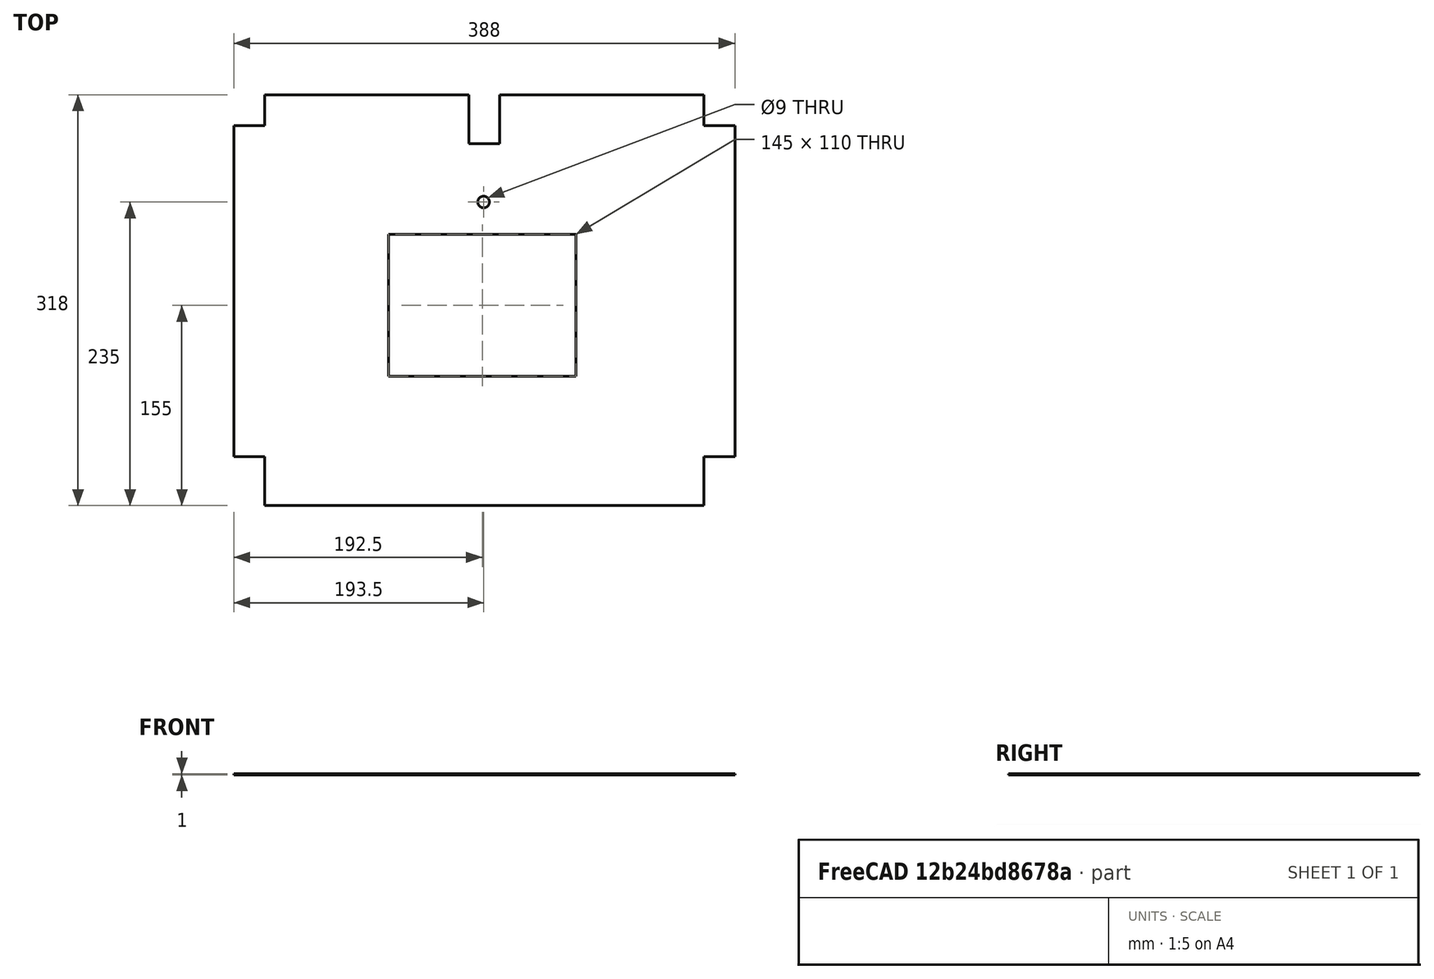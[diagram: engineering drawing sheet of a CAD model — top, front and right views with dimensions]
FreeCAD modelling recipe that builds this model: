
FCSTD DOCUMENT  (FreeCAD 0.15R4671 (Git))
Label: Plataforma
License: All rights reserved
LicenseURL: http://es.wikipedia.org/wiki/Todos_los_derechos_reservados
objects: Part::Box×7, Part::MultiFuse×2, Part::Cylinder×1, Part::Cut×1
note: 11 computed .brp shape members not serialized (recipe doc carries the construction recipe); baked Part::Feature solids carry a one-line shape summary decoded from their .brp

FEATURE [Part::Box] Box  label="Cubo"
  Height = 1
  Length = 388
  Width = 318
FEATURE [Part::Box] Box001  label="Cubo001"
  Height = 1
  Length = 24
  Width = 38
FEATURE [Part::Box] Box002  label="Cubo002"
  Height = 1
  Length = 24
  Placement = pos=(364,0,0) rot=(0,0,1;0rad)
  Width = 38
FEATURE [Part::Box] Box003  label="Cubo003"
  Height = 1
  Length = 24
  Placement = pos=(0,294,0) rot=(0,0,1;0rad)
  Width = 24
FEATURE [Part::Box] Box004  label="Cubo004"
  Height = 1
  Length = 24
  Placement = pos=(364,294,0) rot=(0,0,1;0rad)
  Width = 24
FEATURE [Part::MultiFuse] Fusion  label="huecos esquinas"
  Shapes = -> [Box001,Box002,Box003,Box004]
FEATURE [Part::Box] Box005  label="hueco central"
  Height = 1
  Length = 145
  Placement = pos=(120,100,0) rot=(0,0,1;0rad)
  Width = 110
FEATURE [Part::Box] Box006  label="Cubo005"
  Height = 1
  Length = 24
  Placement = pos=(182,280,0) rot=(0,0,1;0rad)
  Width = 38
FEATURE [Part::Cylinder] Cylinder  label="Cilindro"
  Angle = 360
  Height = 1
  Placement = pos=(193.5,235,0) rot=(0,0,1;0rad)
  Radius = 4.5
FEATURE [Part::MultiFuse] Fusion001  label="cortes"
  Shapes = -> [Fusion,Box005,Box006,Cylinder]
FEATURE [Part::Cut] Cut
  Base = -> Box
  Tool = -> Fusion001
